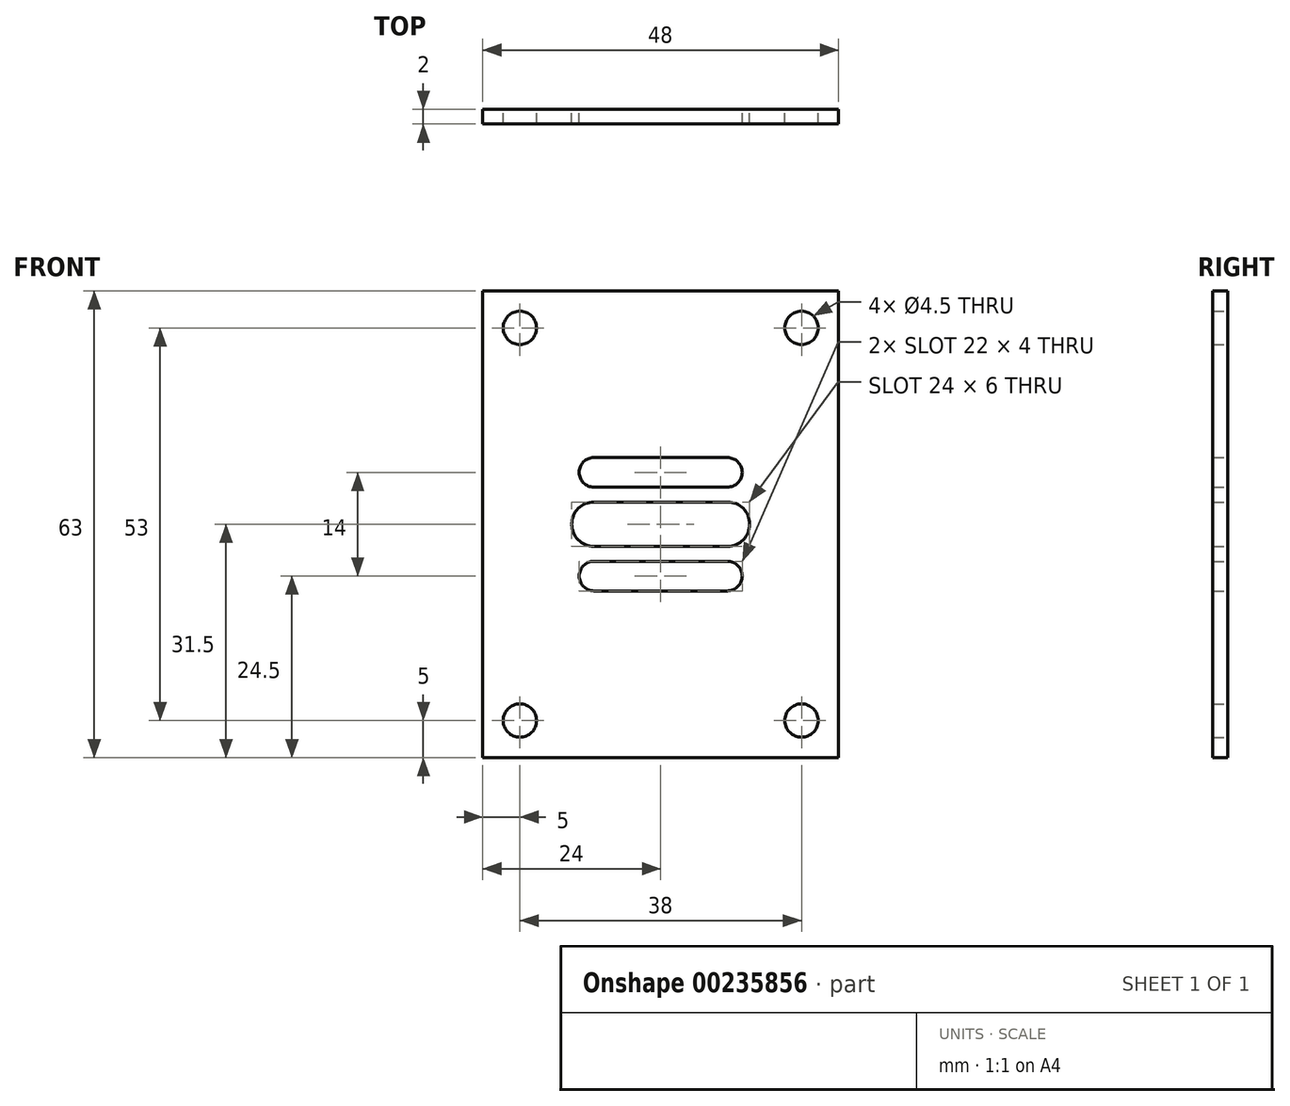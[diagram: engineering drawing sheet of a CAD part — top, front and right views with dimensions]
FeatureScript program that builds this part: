
annotation { "Feature Type Name" : "Feature", "Feature Type Description" : "" }
export const myFeature = defineFeature(function(context is Context, id is Id, definition is map)
    precondition{}
    {
        {
            var Q0;
            Q0=qCreatedBy(makeId("Front.planeOp"),FACE);
            var sketch = newSketch(context, id + "F0", { "sketchPlane" : qUnion([Q0])});
            skLineSegment(sketch, "E0.bottom", {"start": v(-24, 31.5) * mm, "end": v(24, 31.5) * mm});
            skLineSegment(sketch, "E0.top", {"start": v(-24, -31.5) * mm, "end": v(24, -31.5) * mm});
            skLineSegment(sketch, "E0.left", {"start": v(-24, 31.5) * mm, "end": v(-24, -31.5) * mm});
            skLineSegment(sketch, "E0.right", {"start": v(24, 31.5) * mm, "end": v(24, -31.5) * mm});
            skPoint(sketch, "E0.middle", {"position": v(0, 0) * mm});
            skLineSegment(sketch, "E1.bottom", {"start": v(-19, 26.5) * mm, "end": v(19, 26.5) * mm, "construction": true});
            skLineSegment(sketch, "E1.top", {"start": v(-19, -26.5) * mm, "end": v(19, -26.5) * mm, "construction": true});
            skLineSegment(sketch, "E1.left", {"start": v(-19, 26.5) * mm, "end": v(-19, -26.5) * mm, "construction": true});
            skLineSegment(sketch, "E1.right", {"start": v(19, 26.5) * mm, "end": v(19, -26.5) * mm, "construction": true});
            skCircle(sketch, "E2", {"center": v(-19, 26.5) * mm, "radius": 2.25 * mm});
            skCircle(sketch, "E3", {"center": v(19, 26.5) * mm, "radius": 2.25 * mm});
            skCircle(sketch, "E4", {"center": v(19, -26.5) * mm, "radius": 2.25 * mm});
            skCircle(sketch, "E5", {"center": v(-19, -26.5) * mm, "radius": 2.25 * mm});
            skLineSegment(sketch, "E6", {"start": v(-12, 0) * mm, "end": v(12, 0) * mm, "construction": true});
            skLineSegment(sketch, "E7.0", {"start": v(-12, -7) * mm, "end": v(12, -7) * mm, "construction": true});
            skLineSegment(sketch, "E8.0", {"start": v(-12, 7) * mm, "end": v(12, 7) * mm, "construction": true});
            skLineSegment(sketch, "E9.0", {"start": v(-9, -3) * mm, "end": v(9, -3) * mm});
            skLineSegment(sketch, "E10.0", {"start": v(-9, 3) * mm, "end": v(0, 3) * mm});
            skLineSegment(sketch, "E11.0", {"start": v(-9, -9) * mm, "end": v(9, -9) * mm});
            skLineSegment(sketch, "E12.0", {"start": v(-9, -5) * mm, "end": v(9, -5) * mm});
            skLineSegment(sketch, "E13.0", {"start": v(-9, 5) * mm, "end": v(9, 5) * mm});
            skLineSegment(sketch, "E14.0", {"start": v(-9, 9) * mm, "end": v(9, 9) * mm});
            skLineSegment(sketch, "E15", {"start": v(0, 0) * mm, "end": v(0, 15.43) * mm, "construction": true});
            skLineSegment(sketch, "E16.0", {"start": v(12, -9) * mm, "end": v(12, 15.43) * mm, "construction": true});
            skLineSegment(sketch, "E17.0", {"start": v(-12, -9) * mm, "end": v(-12, -3) * mm, "construction": true});
            skPoint(sketch, "E18.orphan", {"position": v(-19, 0) * mm});
            skLineSegment(sketch, "E19", {"start": v(0, 3) * mm, "end": v(9, 3) * mm});
            skLineSegment(sketch, "E20", {"start": v(-12, 0) * mm, "end": v(-12, 0) * mm});
            skLineSegment(sketch, "E21.trimOffspring", {"start": v(-12, 3) * mm, "end": v(-12, 15.43) * mm, "construction": true});
            skPoint(sketch, "E22.visualSharp", {"position": v(-12, 3) * mm});
            skArc(sketch, "E22.filletArc", {"start": v(-9, 3) * mm, "mid": v(-11.12, 2.12) * mm, "end": v(-12, 0) * mm});
            skPoint(sketch, "E23.visualSharp", {"position": v(-12, -3) * mm});
            skArc(sketch, "E23.filletArc", {"start": v(-12, 0) * mm, "mid": v(-11.12, -2.12) * mm, "end": v(-9, -3) * mm});
            skLineSegment(sketch, "E24", {"start": v(12, 0) * mm, "end": v(12, 0) * mm});
            skPoint(sketch, "E25.visualSharp", {"position": v(12, 3) * mm});
            skArc(sketch, "E25.filletArc", {"start": v(12, 0) * mm, "mid": v(11.12, 2.12) * mm, "end": v(9, 3) * mm});
            skPoint(sketch, "E26.visualSharp", {"position": v(12, -3) * mm});
            skArc(sketch, "E26.filletArc", {"start": v(9, -3) * mm, "mid": v(11.12, -2.12) * mm, "end": v(12, 0) * mm});
            skArc(sketch, "E27", {"start": v(-9, -5) * mm, "mid": v(-11, -7) * mm, "end": v(-9, -9) * mm});
            skArc(sketch, "E28", {"start": v(-9, 9) * mm, "mid": v(-11, 7) * mm, "end": v(-9, 5) * mm});
            skArc(sketch, "E29", {"start": v(9, 9) * mm, "mid": v(11, 7) * mm, "end": v(9, 5) * mm});
            skArc(sketch, "E30", {"start": v(9, -5) * mm, "mid": v(11, -7) * mm, "end": v(9, -9) * mm});
            skSolve(sketch);
        }
        {
            var Q0;
            Q0 = qSketchRegion(id + "F0", true);
            extrude(context, id + "F1", {"entities" : qUnion([Q0]), "depth" : 2 * mm, "symmetric" : true});
        }
    });
